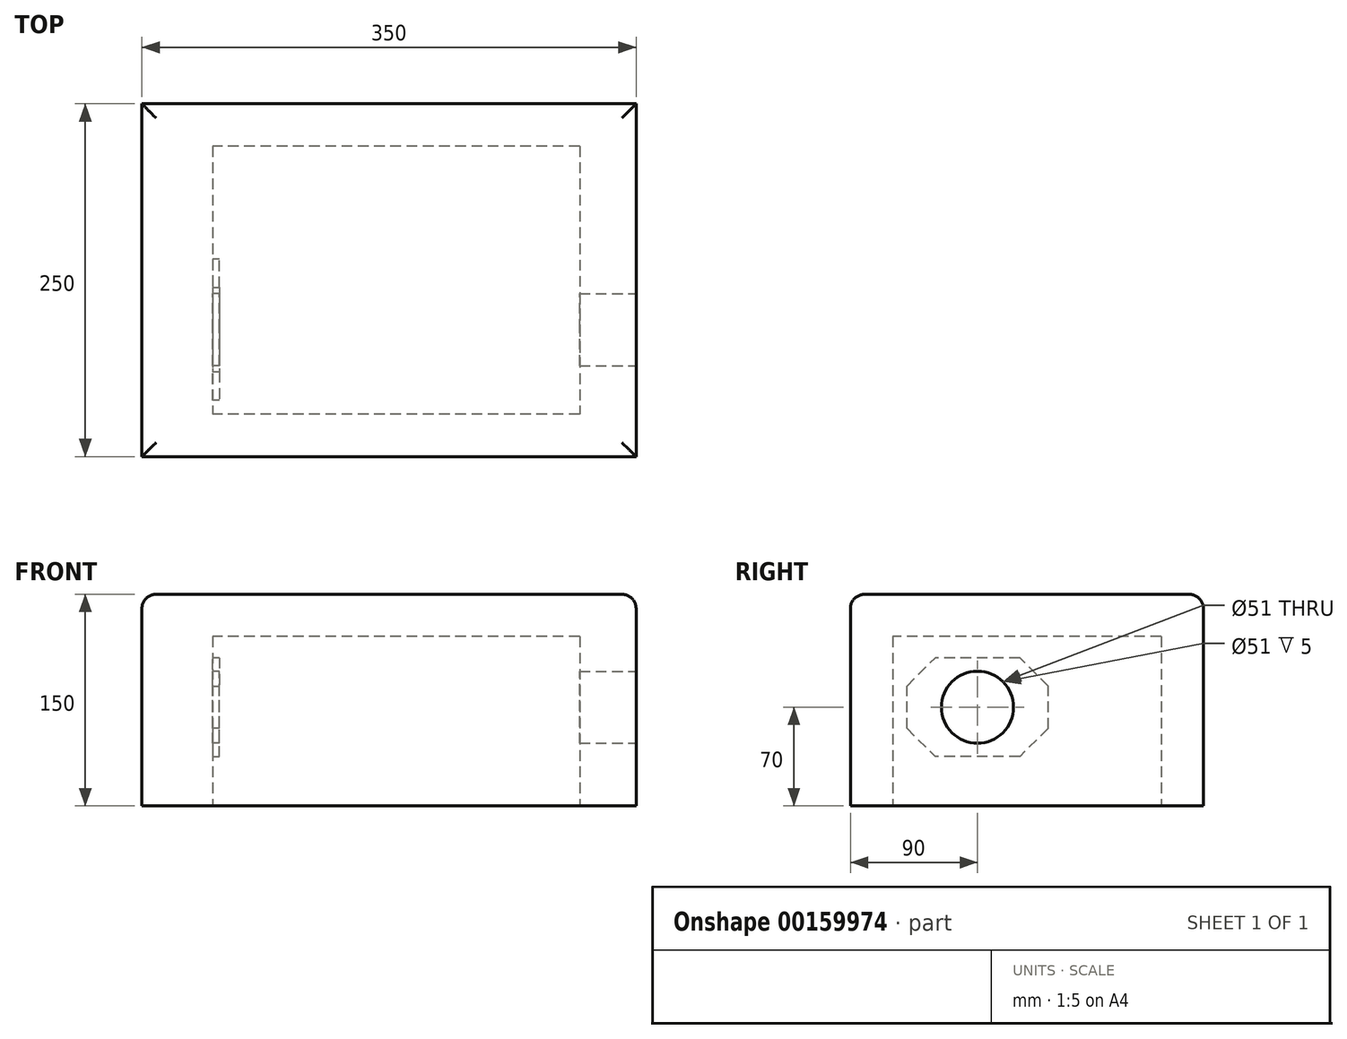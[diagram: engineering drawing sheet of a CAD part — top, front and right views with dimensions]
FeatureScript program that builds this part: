
annotation { "Feature Type Name" : "Feature", "Feature Type Description" : "" }
export const myFeature = defineFeature(function(context is Context, id is Id, definition is map)
    precondition{}
    {
        {
            assignVariable(context, id + "F0", {"name" : "t", "anyValue" : 150 * mm});
        }
        {
            var Q0;
            Q0=qCreatedBy(makeId("Top.planeOp"),FACE);
            var sketch = newSketch(context, id + "F1", { "sketchPlane" : qUnion([Q0])});
            skLineSegment(sketch, "E0.bottom", {"start": v(175, -125) * mm, "end": v(-175, -125) * mm});
            skLineSegment(sketch, "E0.top", {"start": v(175, 125) * mm, "end": v(-175, 125) * mm});
            skLineSegment(sketch, "E0.left", {"start": v(175, -125) * mm, "end": v(175, 125) * mm});
            skLineSegment(sketch, "E0.right", {"start": v(-175, -125) * mm, "end": v(-175, 125) * mm});
            skPoint(sketch, "E0.middle", {"position": v(0, 0) * mm});
            skLineSegment(sketch, "E1.0", {"start": v(173, 123) * mm, "end": v(-125, 123) * mm});
            skLineSegment(sketch, "E1.1", {"start": v(173, -125) * mm, "end": v(173, 123) * mm});
            skSolve(sketch);
        }
        {
            var Q0;
            Q0 = qSketchRegion(id + "F1", true);
            extrude(context, id + "F2", {"entities" : qUnion([Q0]), "oppositeDirection" : true, "depth" : getVariable(context, 't')});
        }
        {
            var Q0;
            Q0=makeQuery(id+"F2.opExtrude","CAP_FACE",FACE,{"disambiguationData":[OSD([sQuery(id+"F1.wireOp",EDGE,"E0.bottom"),sQuery(id+"F1.wireOp",EDGE,"E0.top"),sQuery(id+"F1.wireOp",EDGE,"E0.left"),sQuery(id+"F1.wireOp",EDGE,"E0.right")])],"isStart":false});
            var sketch = newSketch(context, id + "F3", { "sketchPlane" : qUnion([Q0])});
            skLineSegment(sketch, "E2.bottom", {"start": v(135, -95) * mm, "end": v(-125, -95) * mm});
            skLineSegment(sketch, "E2.top", {"start": v(135, 95) * mm, "end": v(-125, 95) * mm});
            skLineSegment(sketch, "E2.left", {"start": v(135, -95) * mm, "end": v(135, 95) * mm});
            skLineSegment(sketch, "E2.right", {"start": v(-125, -95) * mm, "end": v(-125, 95) * mm});
            skPoint(sketch, "E2.middle", {"position": v(5, 0) * mm});
            skSolve(sketch);
        }
        {
            var Q0;
            Q0 = qSketchRegion(id + "F3", true);
            extrude(context, id + "F4", {"entities" : qUnion([Q0]), "operationType" : NewBodyOperationType.REMOVE, "oppositeDirection" : true, "depth" : getVariable(context, 't') - 30 * mm});
        }
        {
            var Q0;
            Q0=makeQuery(id+"F2.opExtrude","SWEPT_FACE",FACE,{"disambiguationData":[OSD([sQuery(id+"F1.wireOp",EDGE,"E0.left")])]});
            var sketch = newSketch(context, id + "F5", { "sketchPlane" : qUnion([Q0])});
            skCircle(sketch, "E3", {"center": v(-35, -80) * mm, "radius": 25.5 * mm});
            skLineSegment(sketch, "E4", {"start": v(-35, -80) * mm, "end": v(0, 0) * mm, "construction": true});
            skSolve(sketch);
        }
        {
            var Q0;
            Q0 = qSketchRegion(id + "F5", true);
            var Q1;
            Q1=makeQuery(id+"F4.boolean.opBoolean","COPY",FACE,{"derivedFrom":makeQuery(id+"F4.opExtrude","SWEPT_FACE",FACE,{"disambiguationData":[OSD([sQuery(id+"F3.wireOp",EDGE,"E2.right")])]})});
            extrude(context, id + "F6", {"entities" : qUnion([Q0]), "operationType" : NewBodyOperationType.REMOVE, "endBound" : BoundingType.UP_TO_SURFACE, "oppositeDirection" : true, "endBoundEntityFace" : qUnion([Q1]), "depth" : 25 * mm});
        }
        {
            var Q0;
            Q0=makeQuery(id+"F2.opExtrude","CAP_EDGE",EDGE,{"disambiguationData":[OSD([sQuery(id+"F1.wireOp",EDGE,"E0.bottom")])],"isStart":true});
            var Q1;
            Q1=makeQuery(id+"F2.opExtrude","CAP_EDGE",EDGE,{"disambiguationData":[OSD([sQuery(id+"F1.wireOp",EDGE,"E0.right")])],"isStart":true});
            var Q2;
            Q2=makeQuery(id+"F2.opExtrude","CAP_EDGE",EDGE,{"disambiguationData":[OSD([sQuery(id+"F1.wireOp",EDGE,"E0.top")])],"isStart":true});
            var Q3;
            Q3=makeQuery(id+"F2.opExtrude","CAP_EDGE",EDGE,{"disambiguationData":[OSD([sQuery(id+"F1.wireOp",EDGE,"E0.left")])],"isStart":true});
            fillet(context, id + "F7", {"entities" : qUnion([Q0, Q1, Q2, Q3]), "radius" : 10 * mm, "tangentPropagation" : true, "allowEdgeOverflow" : false});
        }
        {
            var Q0;
            Q0=makeQuery(id+"F4.boolean.opBoolean","COPY",FACE,{"derivedFrom":makeQuery(id+"F4.opExtrude","SWEPT_FACE",FACE,{"disambiguationData":[OSD([sQuery(id+"F3.wireOp",EDGE,"E2.right")])]})});
            var sketch = newSketch(context, id + "F8", { "sketchPlane" : qUnion([Q0])});
            skCircle(sketch, "E5.0", {"center": v(-35, -80) * mm, "radius": 25.5 * mm});
            skLineSegment(sketch, "E6.bottom", {"start": v(15, -115) * mm, "end": v(-85, -115) * mm});
            skLineSegment(sketch, "E6.top", {"start": v(15, -45) * mm, "end": v(-85, -45) * mm});
            skLineSegment(sketch, "E6.left", {"start": v(15, -115) * mm, "end": v(15, -45) * mm});
            skLineSegment(sketch, "E6.right", {"start": v(-85, -115) * mm, "end": v(-85, -45) * mm});
            skSolve(sketch);
        }
        {
            var Q0;
            Q0 = qSketchRegion(id + "F8", true);
            extrude(context, id + "F9", {"entities" : qUnion([Q0]), "operationType" : NewBodyOperationType.ADD, "depth" : 5 * mm});
        }
        {
            var Q0;
            Q0=makeQuery(id+"F9.opExtrude","SWEPT_EDGE",EDGE,{"disambiguationData":[OSD([sQuery(id+"F8.wireOp",EDGE,"E6.bottom"),sQuery(id+"F8.wireOp",EDGE,"E6.right")])]});
            var Q1;
            Q1=makeQuery(id+"F9.opExtrude","SWEPT_EDGE",EDGE,{"disambiguationData":[OSD([sQuery(id+"F8.wireOp",EDGE,"E6.top"),sQuery(id+"F8.wireOp",EDGE,"E6.right")])]});
            var Q2;
            Q2=makeQuery(id+"F9.opExtrude","SWEPT_EDGE",EDGE,{"disambiguationData":[OSD([sQuery(id+"F8.wireOp",EDGE,"E6.bottom"),sQuery(id+"F8.wireOp",EDGE,"E6.left")])]});
            var Q3;
            Q3=makeQuery(id+"F9.opExtrude","SWEPT_EDGE",EDGE,{"disambiguationData":[OSD([sQuery(id+"F8.wireOp",EDGE,"E6.top"),sQuery(id+"F8.wireOp",EDGE,"E6.left")])]});
            chamfer(context, id + "F10", {"entities" : qUnion([Q0, Q1, Q2, Q3]), "width" : 20 * mm, "tangentPropagation" : true});
        }
    });
